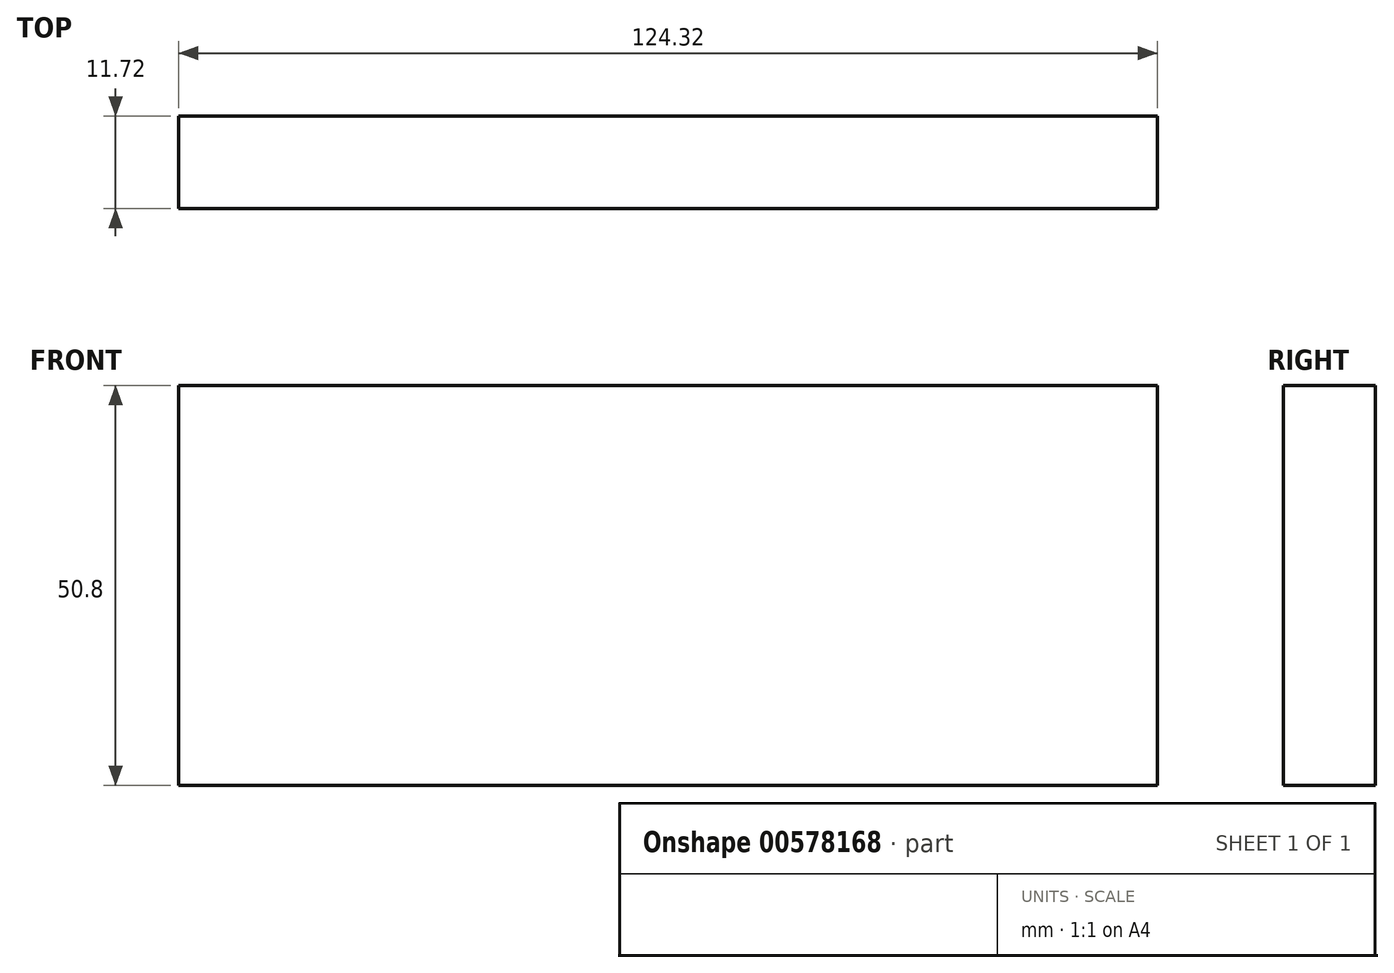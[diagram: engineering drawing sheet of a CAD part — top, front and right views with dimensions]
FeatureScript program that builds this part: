
annotation { "Feature Type Name" : "Feature", "Feature Type Description" : "" }
export const myFeature = defineFeature(function(context is Context, id is Id, definition is map)
    precondition{}
    {
        {
            var Q0;
            Q0=qCreatedBy(makeId("Top.planeOp"),FACE);
            var sketch = newSketch(context, id + "F0", { "sketchPlane" : qUnion([Q0])});
            skLineSegment(sketch, "E0.bottom", {"start": v(-64.04, 49.42) * mm, "end": v(67.9, 49.42) * mm});
            skLineSegment(sketch, "E0.top", {"start": v(-64.04, 30.08) * mm, "end": v(67.9, 30.08) * mm});
            skLineSegment(sketch, "E0.left", {"start": v(-64.04, 49.42) * mm, "end": v(-64.04, 30.08) * mm});
            skLineSegment(sketch, "E0.right", {"start": v(67.9, 49.42) * mm, "end": v(67.9, 30.08) * mm});
            skLineSegment(sketch, "E1.0", {"start": v(-60.23, 45.61) * mm, "end": v(64.1, 45.61) * mm});
            skLineSegment(sketch, "E1.1", {"start": v(-60.23, 45.61) * mm, "end": v(-60.23, 33.9) * mm});
            skLineSegment(sketch, "E1.2", {"start": v(-60.23, 33.9) * mm, "end": v(64.1, 33.9) * mm});
            skLineSegment(sketch, "E1.3", {"start": v(64.1, 45.61) * mm, "end": v(64.1, 33.9) * mm});
            skSolve(sketch);
        }
        {
            var Q0;
            Q0=makeQuery(id+"F0.imprint","IMPRINT",FACE,{"disambiguationData":[TD([[makeQuery(id+"F0.imprint","IMPRINT",EDGE,{"derivedFrom":sQuery(id+"F0.wireOp",EDGE,"E1.0")}),-1.0]])]});
            extrude(context, id + "F1", {"entities" : qUnion([Q0]), "depth" : 25.4 * mm, "offsetDistance" : 25.4 * mm});
        }
        {
            var Q0;
            Q0=makeQuery(id+"F1.opExtrude","CAP_FACE",FACE,{"disambiguationData":[OSD([sQuery(id+"F0.wireOp",EDGE,"E1.0"),sQuery(id+"F0.wireOp",EDGE,"E1.1"),sQuery(id+"F0.wireOp",EDGE,"E1.2"),sQuery(id+"F0.wireOp",EDGE,"E1.3")])],"isStart":false});
            var sketch = newSketch(context, id + "F2", { "sketchPlane" : qUnion([Q0])});
            skLineSegment(sketch, "E2.bottom", {"start": v(-60.23, 45.61) * mm, "end": v(64.1, 45.61) * mm});
            skLineSegment(sketch, "E2.top", {"start": v(-60.23, 33.9) * mm, "end": v(64.1, 33.9) * mm});
            skLineSegment(sketch, "E2.left", {"start": v(-60.23, 45.61) * mm, "end": v(-60.23, 33.9) * mm});
            skLineSegment(sketch, "E2.right", {"start": v(64.1, 45.61) * mm, "end": v(64.1, 33.9) * mm});
            skSolve(sketch);
        }
        {
            var Q0;
            Q0=makeQuery(id+"F2.imprint","IMPRINT",FACE,{"disambiguationData":[TD([[makeQuery(id+"F2.imprint","IMPRINT",EDGE,{"derivedFrom":sQuery(id+"F2.wireOp",EDGE,"E2.bottom")}),-1.0]])]});
            var sketch = newSketch(context, id + "F3", { "sketchPlane" : qUnion([Q0])});
            skSolve(sketch);
        }
        {
            var Q0;
            Q0 = qSketchRegion(id + "F3", true);
            var Q1;
            Q1=makeQuery(id+"F2.imprint","IMPRINT",FACE,{"disambiguationData":[TD([[makeQuery(id+"F2.imprint","IMPRINT",EDGE,{"derivedFrom":sQuery(id+"F2.wireOp",EDGE,"E2.bottom")}),-1.0]])]});
            extrude(context, id + "F4", {"entities" : qUnion([Q0, Q1]), "operationType" : NewBodyOperationType.ADD, "depth" : 25.4 * mm, "offsetDistance" : 25.4 * mm});
        }
    });
